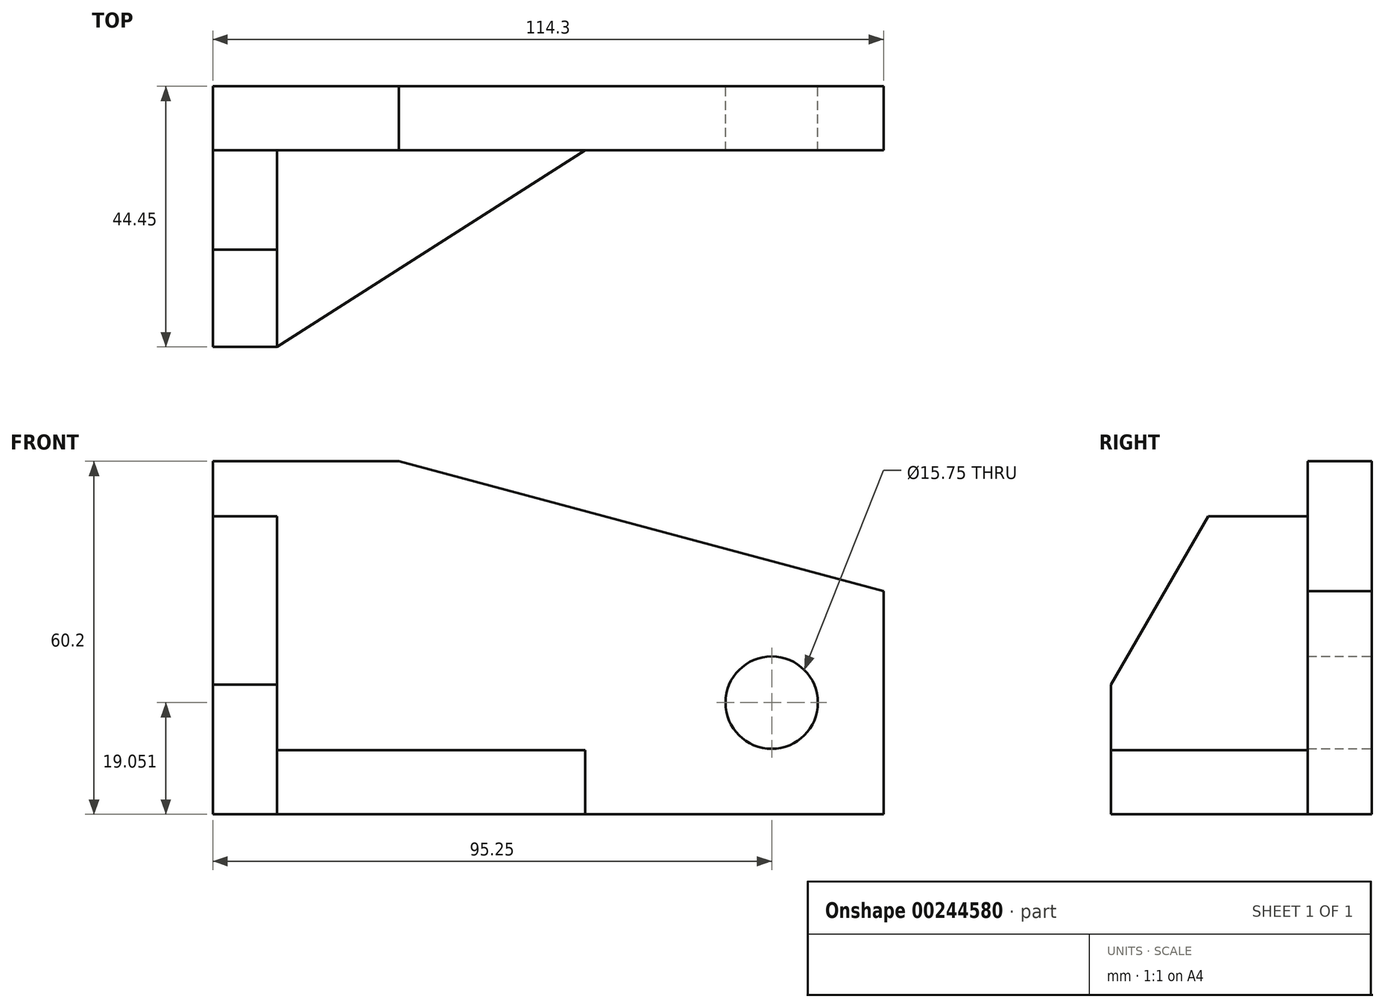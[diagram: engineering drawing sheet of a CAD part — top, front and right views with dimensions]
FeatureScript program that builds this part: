
annotation { "Feature Type Name" : "Feature", "Feature Type Description" : "" }
export const myFeature = defineFeature(function(context is Context, id is Id, definition is map)
    precondition{}
    {
        {
            var Q0;
            Q0=qCreatedBy(makeId("Front.planeOp"),FACE);
            var sketch = newSketch(context, id + "F0", { "sketchPlane" : qUnion([Q0])});
            skLineSegment(sketch, "E0.bottom", {"start": v(57.15, -30.1) * mm, "end": v(-57.15, -30.1) * mm});
            skLineSegment(sketch, "E0.top", {"start": v(-25.4, 30.1) * mm, "end": v(-57.15, 30.1) * mm});
            skLineSegment(sketch, "E0.left", {"start": v(57.15, -30.1) * mm, "end": v(57.15, 7.98) * mm});
            skLineSegment(sketch, "E0.right", {"start": v(-57.15, -30.1) * mm, "end": v(-57.15, 30.1) * mm});
            skPoint(sketch, "E0.middle", {"position": v(0, 0) * mm});
            skLineSegment(sketch, "E1", {"start": v(-25.4, 30.1) * mm, "end": v(57.15, 7.98) * mm});
            skPoint(sketch, "E2.orphan", {"position": v(57.15, 30.1) * mm});
            skCircle(sketch, "E3", {"center": v(38.1, -11.05) * mm, "radius": 7.87 * mm});
            skPoint(sketch, "E4", {"position": v(57.15, -30.1) * mm});
            skSolve(sketch);
        }
        {
            var Q0;
            Q0=makeQuery(id+"F0.imprint","IMPRINT",FACE,{"disambiguationData":[TD([[makeQuery(id+"F0.imprint","IMPRINT",EDGE,{"derivedFrom":sQuery(id+"F0.wireOp",EDGE,"E0.bottom")}),-1.0]])]});
            extrude(context, id + "F1", {"entities" : qUnion([Q0]), "depth" : 10.92 * mm});
        }
        {
            var Q0;
            Q0=qCreatedBy(makeId("Front.planeOp"),FACE);
            var sketch = newSketch(context, id + "F2", { "sketchPlane" : qUnion([Q0])});
            skLineSegment(sketch, "E5", {"start": v(-57.15, 20.7) * mm, "end": v(-57.15, -30.1) * mm});
            skLineSegment(sketch, "E6", {"start": v(-57.15, -30.1) * mm, "end": v(-46.23, -30.1) * mm});
            skLineSegment(sketch, "E7", {"start": v(-46.23, -30.1) * mm, "end": v(-46.23, 20.7) * mm});
            skLineSegment(sketch, "E8", {"start": v(-46.23, 20.7) * mm, "end": v(-57.15, 20.7) * mm});
            skSolve(sketch);
        }
        {
            var Q0;
            Q0 = qSketchRegion(id + "F2", true);
            extrude(context, id + "F3", {"entities" : qUnion([Q0]), "operationType" : NewBodyOperationType.ADD, "depth" : 44.45 * mm});
        }
        {
            var Q0;
            Q0=makeQuery(id+"F3.opExtrude","CAP_EDGE",EDGE,{"disambiguationData":[OSD([sQuery(id+"F2.wireOp",EDGE,"E8")])],"isStart":false});
            chamfer(context, id + "F4", {"entities" : qUnion([Q0]), "chamferType" : ChamferType.TWO_OFFSETS, "width1" : 28.7 * mm, "oppositeDirection" : false, "width2" : 16.57 * mm, "tangentPropagation" : true});
        }
        {
            var Q0;
            Q0=qCreatedBy(makeId("Front.planeOp"),FACE);
            var sketch = newSketch(context, id + "F5", { "sketchPlane" : qUnion([Q0])});
            skLineSegment(sketch, "E9.bottom", {"start": v(-46.23, -19.18) * mm, "end": v(6.35, -19.18) * mm});
            skLineSegment(sketch, "E9.top", {"start": v(-46.23, -30.1) * mm, "end": v(6.35, -30.1) * mm});
            skLineSegment(sketch, "E9.left", {"start": v(-46.23, -19.18) * mm, "end": v(-46.23, -30.1) * mm});
            skLineSegment(sketch, "E9.right", {"start": v(6.35, -19.18) * mm, "end": v(6.35, -30.1) * mm});
            skSolve(sketch);
        }
        {
            var Q0;
            Q0=makeQuery(id+"F5.imprint","IMPRINT",FACE,{"disambiguationData":[TD([[makeQuery(id+"F5.imprint","IMPRINT",EDGE,{"derivedFrom":sQuery(id+"F5.wireOp",EDGE,"E9.bottom")}),-1.0]])]});
            extrude(context, id + "F6", {"entities" : qUnion([Q0]), "operationType" : NewBodyOperationType.ADD, "depth" : 44.45 * mm});
        }
        {
            var Q0;
            Q0=makeQuery(id+"F6.opExtrude","CAP_EDGE",EDGE,{"disambiguationData":[OSD([sQuery(id+"F5.wireOp",EDGE,"E9.right")])],"isStart":false});
            chamfer(context, id + "F7", {"entities" : qUnion([Q0]), "chamferType" : ChamferType.TWO_OFFSETS, "width1" : 33.53 * mm, "oppositeDirection" : false, "width2" : 52.58 * mm, "tangentPropagation" : true});
        }
    });
